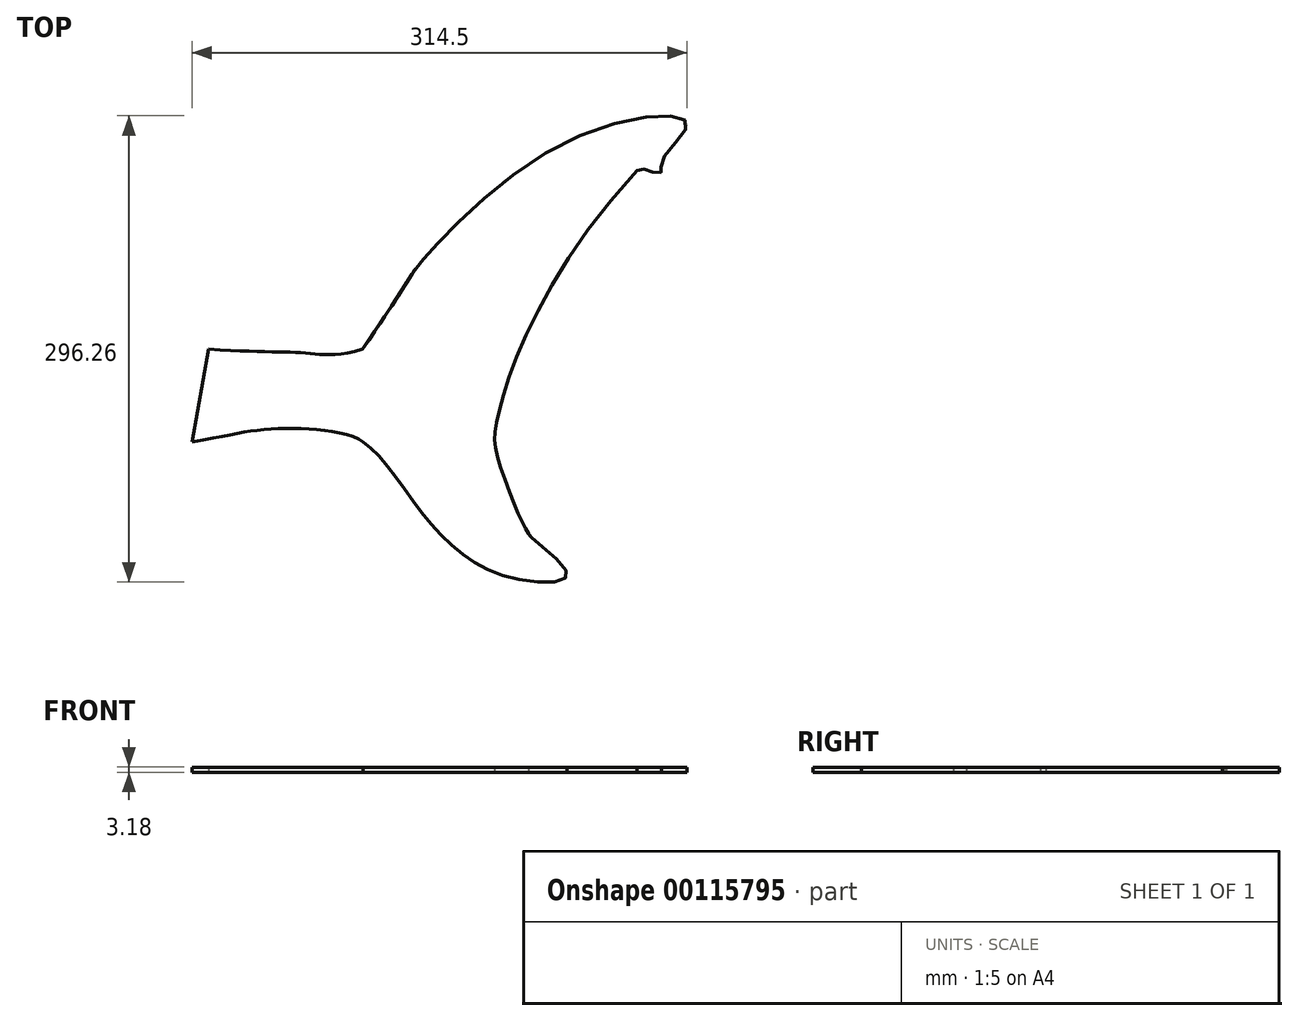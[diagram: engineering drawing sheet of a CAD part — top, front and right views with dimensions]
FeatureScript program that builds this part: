
annotation { "Feature Type Name" : "Feature", "Feature Type Description" : "" }
export const myFeature = defineFeature(function(context is Context, id is Id, definition is map)
    precondition{}
    {
        {
            var Q0;
            Q0=qCreatedBy(makeId("Top.planeOp"),FACE);
            var sketch = newSketch(context, id + "F0", { "sketchPlane" : qUnion([Q0])});
            skFitSpline(sketch, "E0", {"points": [v(-172.23, 58.11) * mm, v(-155.79, 41.72) * mm, v(-134.94, 13.28) * mm, v(-109.46, -12.84) * mm, v(-72.74, -29.4) * mm, v(-42.48, -25.76) * mm, v(-66.75, -0.9) * mm, v(-67.09, -0.25) * mm], "startDerivative": vector(97.89, -66.39) * mm, "endDerivative": vector(0, -31.6) * mm});
            skFitSpline(sketch, "E1", {"points": [v(-67.09, -0.25) * mm, v(-74.44, 14.5) * mm, v(-87.43, 51) * mm, v(-87.43, 70.24) * mm, v(1.76, 230.54) * mm], "startDerivative": vector(-44.31, 73.19) * mm, "endDerivative": vector(404.27, 443.47) * mm});
            skFitSpline(sketch, "E2", {"points": [v(1.76, 230.54) * mm, v(8.18, 230.54) * mm, v(17.22, 229.38) * mm, v(17.22, 235.67) * mm, v(33.65, 259.76) * mm, v(-43, 248.62) * mm, v(-136.88, 170.38) * mm, v(-172.53, 116.92) * mm], "startDerivative": vector(137, 88.61) * mm, "endDerivative": vector(-567.88, -827) * mm});
            skFitSpline(sketch, "E3", {"points": [v(-172.53, 116.92) * mm, v(-208.6, 114.54) * mm, v(-270.21, 116.92) * mm], "startDerivative": vector(-120.75, -36.12) * mm, "endDerivative": vector(-171.54, 11.4) * mm});
            skFitSpline(sketch, "E4", {"points": [v(-172.23, 58.11) * mm, v(-201.37, 65.85) * mm, v(-237.83, 65.63) * mm, v(-280.85, 58.11) * mm], "startDerivative": vector(-59.13, 44.28) * mm, "endDerivative": vector(-177.23, -30.5) * mm});
            skLineSegment(sketch, "E5", {"start": v(-270.21, 116.92) * mm, "end": v(-280.85, 58.11) * mm});
            skSolve(sketch);
        }
        {
            var Q0;
            Q0=makeQuery(id+"F0.imprint","IMPRINT",FACE,{"disambiguationData":[TD([[makeQuery(id+"F0.imprint","IMPRINT",EDGE,{"derivedFrom":sQuery(id+"F0.wireOp",EDGE,"E0")}),1.0]])]});
            extrude(context, id + "F1", {"entities" : qUnion([Q0]), "depth" : 3.17 * mm});
        }
    });
